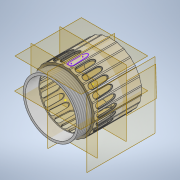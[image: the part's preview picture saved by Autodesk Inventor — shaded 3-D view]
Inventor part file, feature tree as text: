
AUTODESK INVENTOR PART (.ipt)
format: ipt  version: 2020.2 (Build 242310000, 310)  size: 1,818,624 bytes
history: native  units: mm
features: sketch x16, extrude x11, plane x10, thread x4, chamfer x3, pattern_circular x2, emboss x1, revolve x1, mirror x1, split x1
ambient origin geometry x8: Origin, YZ Plane, XZ Plane, XY Plane, X Axis, Y Axis, Z Axis, Center Point
bodies: Solid1 (feature_tree), Solid2 (feature_tree), Solid3 (feature_tree)
feature tree (50):
  extrude  "Extrusion1"  Depth=1.6mm
  plane  "Work Plane1"
  sketch  "Sketch2"  dims[d2=4.714404mm d3=0.428883mm d4=250.0mm d6=360.0deg d8=45.0mm d9=0.0mm d11=10.0mm d12=0.0mm]
  extrude  "Extrusion2"  Depth=10.0mm
  chamfer  "Chamfer1"  Distance=250.0mm Angle=360.0deg
  chamfer  "Chamfer2"  Distance=45.0mm
  chamfer  "Chamfer3"  Distance=10.0mm
  extrude  "Extrusion3"  Depth=10.0mm TaperAngle=360.0deg
  pattern_circular  "Circular Pattern1"  Angle=90.0deg  [1 undecoded]
  sketch  "Sketch5"  dims[d18=0.9mm d19=2.0mm d20=45.0deg]
  extrude  "Extrusion4"  Depth=10.0mm TaperAngle=360.0deg
  extrude  "Extrusion5"  Depth=10.0mm TaperAngle=0.0deg
  plane  "Work Plane3"
  plane  "Work Plane4"
  extrude  "Extrusion6"  Depth=10.0mm TaperAngle=0.0deg
  plane  "Work Plane7"
  plane  "Work Plane8"
  sketch  "Sketch7"  dims[d24=0.2mm d25=2.0mm d26=45.0deg]
  plane  "Work Plane9"
  emboss  "Emboss1"
  sketch  "Sketch10"  dims[d29=20.022194mm]
  revolve  "Revolution1"  [1 undecoded]
  pattern_circular  "Circular Pattern2"  [2 undecoded]
  extrude  "Extrusion7"  Depth=10.0mm TaperAngle=0.0deg
  sketch  "Sketch13"  dims[d32=35.0mm d33=0.0mm]
  extrude  "Extrusion8"  Depth=10.0mm
  mirror  "Mirror1"
  thread  "Thread1"  [1 undecoded]
  thread  "Thread2"  [1 undecoded]
  extrude  "Extrusion9"  Depth=0.02mm
  extrude  "Extrusion10"  Depth=10.0mm
  thread  "Thread3"  [1 undecoded]
  plane  "Work Plane10"
  plane  "Work Plane11"
  split  "Split1"
  extrude  "Extrusion11"  Depth=10.0mm TaperAngle=0.0deg
  thread  "Thread4"  [1 undecoded]
  sketch  "Sketch1"  dims[d0=45.0mm d1=1.6mm]
  sketch  "Sketch4"  dims[d13=10.0mm d14=0.0mm d15=250.0mm d16=360.0deg]
  sketch  "Sketch6"  dims[d21=0.9mm d22=2.0mm d23=45.0deg]
  plane  "Work Plane5"
  plane  "Work Plane6"
  sketch  "Sketch9"  dims[d27=10.0mm d28=0.0mm]
  sketch  "Sketch11"  dims[d30=1.170635mm]
  sketch  "Sketch12"  dims[d31=2.0mm]
  sketch  "Sketch14"  dims[d34=90.0deg]
  sketch  "Sketch15"  dims[d35=4.0mm d36=0.0mm]
  sketch  "Sketch16"  dims[d37=11.75mm]
  sketch  "Sketch17"  dims[d38=-16.0mm d39=8.7mm d40=-8.7mm]
  sketch  "Sketch19"  dims[d41=0.2mm d42=0.0mm d43=90.0deg d44=40.0mm d45=360.0deg d47=10.0mm d48=0.0mm d49=9.1mm d50=0.0mm d51=9.1mm d52=0.0mm d53=9.1mm d54=0.0mm d55=1.5mm d56=0.0mm d57=1.133755mm d58=10.0mm d59=0.0mm d60=8.847mm d61=0.0mm d62=21.5mm d63=30.0mm d64=0.02mm d65=1.7mm d66=0.01mm d67=10.0mm d68=0.0mm d69=10.0mm d70=0.0mm]
note: 8 required parameter values undecoded (feature->parameter linkage not recoverable at this tier; creation-order binding heuristic only, values carry confidence <= 0.55)